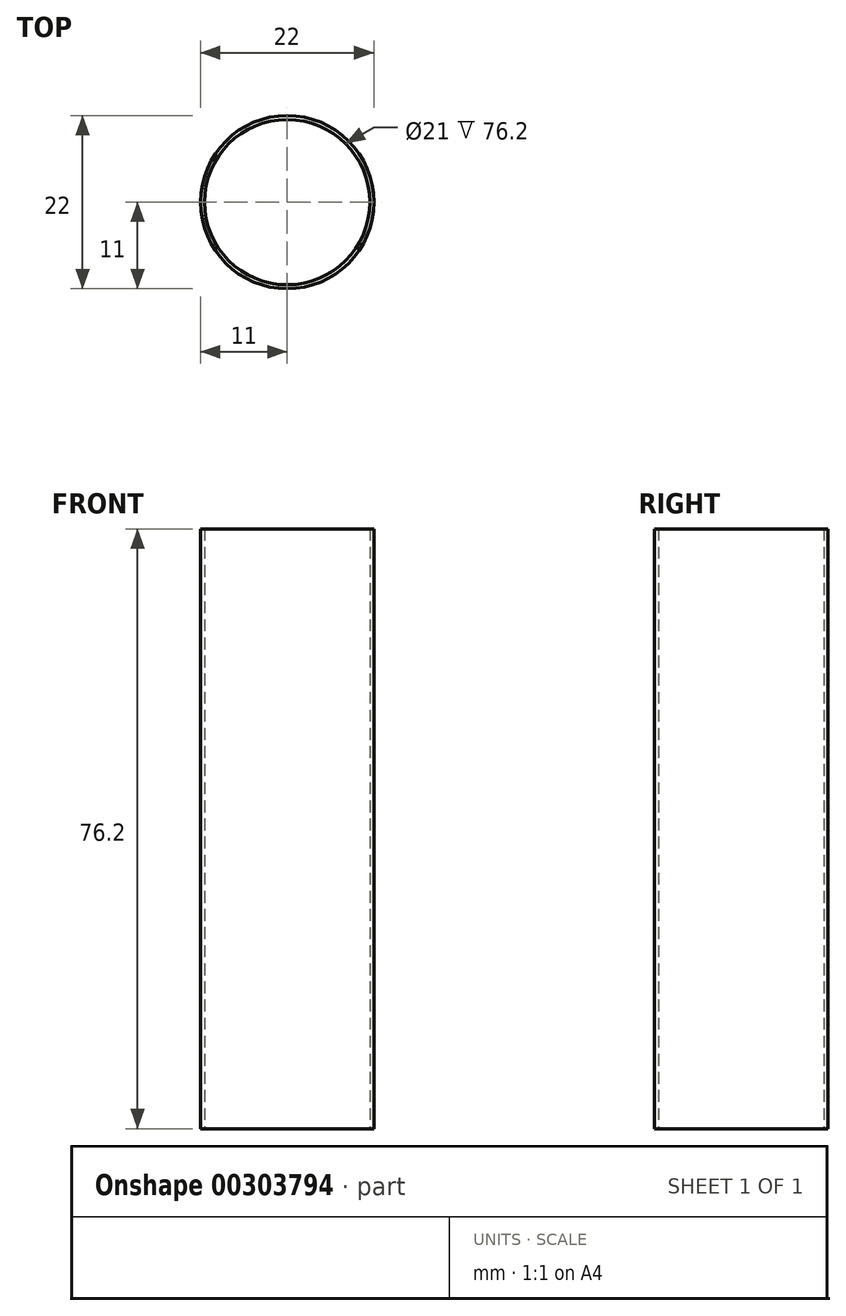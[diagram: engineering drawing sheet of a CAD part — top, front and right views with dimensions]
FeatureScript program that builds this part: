
annotation { "Feature Type Name" : "Feature", "Feature Type Description" : "" }
export const myFeature = defineFeature(function(context is Context, id is Id, definition is map)
    precondition{}
    {
        {
            var Q0;
            Q0=qCreatedBy(makeId("Top.planeOp"),FACE);
            var sketch = newSketch(context, id + "F0", { "sketchPlane" : qUnion([Q0])});
            skCircle(sketch, "E0", {"center": v(0, 0) * mm, "radius": 11 * mm});
            skCircle(sketch, "E1", {"center": v(0, 0) * mm, "radius": 10.5 * mm});
            skSolve(sketch);
        }
        {
            var Q0;
            Q0=makeQuery(id+"F0.imprint","IMPRINT",FACE,{"disambiguationData":[TD([[makeQuery(id+"F0.imprint","IMPRINT",EDGE,{"derivedFrom":sQuery(id+"F0.wireOp",EDGE,"E0")}),1.0]])]});
            extrude(context, id + "F1", {"entities" : qUnion([Q0]), "depth" : 76.2 * mm, "offsetDistance" : 25 * mm});
        }
    });
